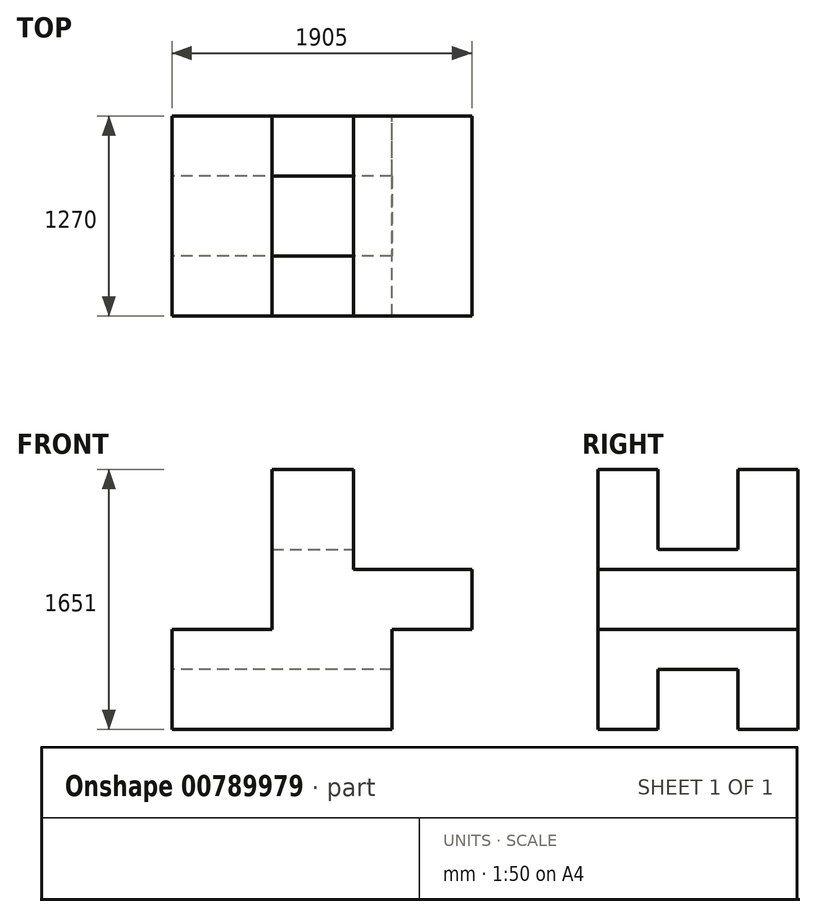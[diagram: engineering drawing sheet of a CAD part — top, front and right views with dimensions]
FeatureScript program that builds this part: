
annotation { "Feature Type Name" : "Feature", "Feature Type Description" : "" }
export const myFeature = defineFeature(function(context is Context, id is Id, definition is map)
    precondition{}
    {
        {
            var Q0;
            Q0=qCreatedBy(makeId("Front.planeOp"),FACE);
            var sketch = newSketch(context, id + "F0", { "sketchPlane" : qUnion([Q0])});
            skLineSegment(sketch, "E0", {"start": v(0, 0) * mm, "end": v(-635, 0) * mm});
            skLineSegment(sketch, "E1", {"start": v(-635, 0) * mm, "end": v(-635, -635) * mm});
            skLineSegment(sketch, "E2", {"start": v(-635, -635) * mm, "end": v(762, -635) * mm});
            skLineSegment(sketch, "E3", {"start": v(762, -635) * mm, "end": v(762, 0) * mm});
            skLineSegment(sketch, "E4", {"start": v(762, 0) * mm, "end": v(1270, 0) * mm});
            skLineSegment(sketch, "E5", {"start": v(1270, 0) * mm, "end": v(1270, 381) * mm});
            skLineSegment(sketch, "E6", {"start": v(1270, 381) * mm, "end": v(518.7, 381) * mm});
            skLineSegment(sketch, "E7", {"start": v(518.7, 381) * mm, "end": v(518.7, 1016) * mm});
            skLineSegment(sketch, "E8", {"start": v(518.7, 1016) * mm, "end": v(0, 1016) * mm});
            skLineSegment(sketch, "E9", {"start": v(0, 1016) * mm, "end": v(0, 0) * mm});
            skSolve(sketch);
        }
        {
            var Q0;
            Q0=makeQuery(id+"F0.imprint","IMPRINT",FACE,{"disambiguationData":[TD([[makeQuery(id+"F0.imprint","IMPRINT",EDGE,{"derivedFrom":sQuery(id+"F0.wireOp",EDGE,"E0")}),1.0]])]});
            extrude(context, id + "F1", {"entities" : qUnion([Q0]), "endBound" : BoundingType.SYMMETRIC, "depth" : 1270 * mm, "offsetDistance" : 25.4 * mm});
        }
        {
            var Q0;
            Q0=makeQuery(id+"F1.opExtrude","SWEPT_FACE",FACE,{"disambiguationData":[OSD([sQuery(id+"F0.wireOp",EDGE,"E8")])]});
            var sketch = newSketch(context, id + "F2", { "sketchPlane" : qUnion([Q0])});
            skLineSegment(sketch, "E10", {"start": v(0, -254) * mm, "end": v(518.7, -254) * mm});
            skLineSegment(sketch, "E11", {"start": v(518.7, -254) * mm, "end": v(518.7, 254) * mm});
            skLineSegment(sketch, "E12", {"start": v(518.7, 254) * mm, "end": v(0, 254) * mm});
            skLineSegment(sketch, "E13", {"start": v(0, 254) * mm, "end": v(0, -254) * mm});
            skLineSegment(sketch, "E14", {"start": v(0, 254) * mm, "end": v(0, 635) * mm});
            skLineSegment(sketch, "E15", {"start": v(0, 635) * mm, "end": v(518.7, 635) * mm});
            skLineSegment(sketch, "E16", {"start": v(518.7, 635) * mm, "end": v(518.7, 254) * mm});
            skLineSegment(sketch, "E17", {"start": v(0, -254) * mm, "end": v(0, -635) * mm});
            skSolve(sketch);
        }
        {
            var Q0;
            Q0=makeQuery(id+"F2.imprint","IMPRINT",FACE,{"disambiguationData":[TD([[makeQuery(id+"F2.imprint","IMPRINT",EDGE,{"derivedFrom":sQuery(id+"F2.wireOp",EDGE,"E10")}),1.0]])]});
            extrude(context, id + "F3", {"entities" : qUnion([Q0]), "operationType" : NewBodyOperationType.REMOVE, "oppositeDirection" : true, "depth" : 508 * mm, "offsetDistance" : 25.4 * mm});
        }
        {
            var Q0;
            Q0=makeQuery(id+"F1.opExtrude","SWEPT_FACE",FACE,{"disambiguationData":[OSD([sQuery(id+"F0.wireOp",EDGE,"E1")])]});
            var sketch = newSketch(context, id + "F4", { "sketchPlane" : qUnion([Q0])});
            skLineSegment(sketch, "E18", {"start": v(-254, -635) * mm, "end": v(-254, -254) * mm});
            skLineSegment(sketch, "E19", {"start": v(-254, -254) * mm, "end": v(254, -254) * mm});
            skLineSegment(sketch, "E20", {"start": v(254, -254) * mm, "end": v(254, -635) * mm});
            skLineSegment(sketch, "E21", {"start": v(254, -635) * mm, "end": v(635, -635) * mm});
            skLineSegment(sketch, "E22", {"start": v(-254, -635) * mm, "end": v(254, -635) * mm});
            skLineSegment(sketch, "E23", {"start": v(-254, -635) * mm, "end": v(-635, -635) * mm});
            skSolve(sketch);
        }
        {
            var Q0;
            Q0=makeQuery(id+"F4.imprint","IMPRINT",FACE,{"disambiguationData":[TD([[makeQuery(id+"F4.imprint","IMPRINT",EDGE,{"derivedFrom":sQuery(id+"F4.wireOp",EDGE,"E18")}),-1.0]])]});
            extrude(context, id + "F5", {"entities" : qUnion([Q0]), "operationType" : NewBodyOperationType.REMOVE, "endBound" : BoundingType.THROUGH_ALL, "oppositeDirection" : true, "depth" : 25.4 * mm, "offsetDistance" : 25.4 * mm});
        }
    });
